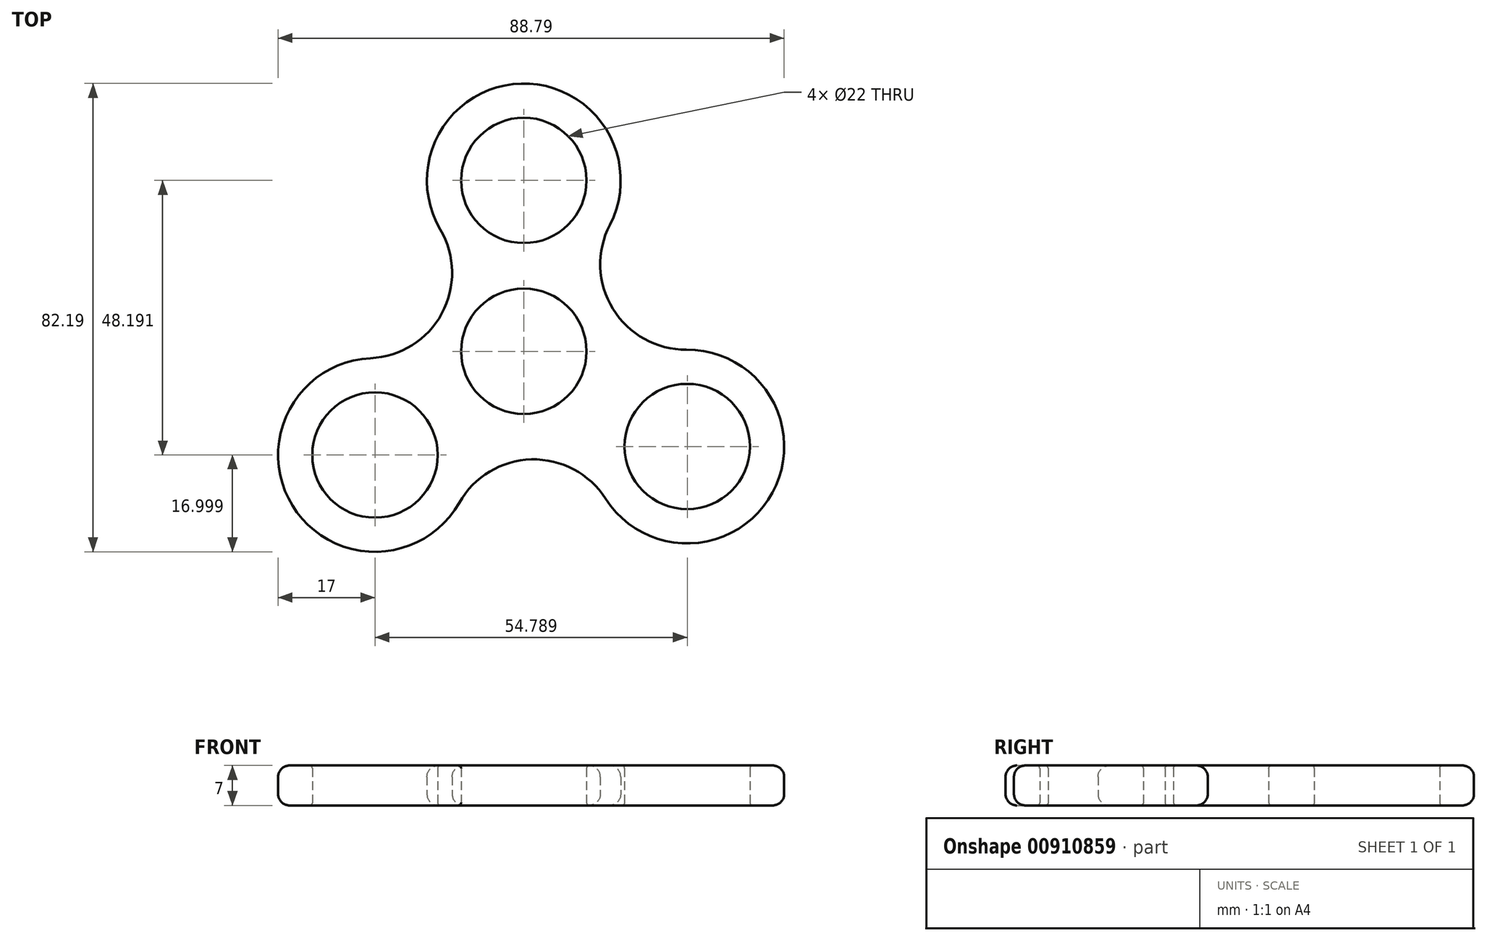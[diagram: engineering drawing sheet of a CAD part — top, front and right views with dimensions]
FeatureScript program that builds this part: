
annotation { "Feature Type Name" : "Feature", "Feature Type Description" : "" }
export const myFeature = defineFeature(function(context is Context, id is Id, definition is map)
    precondition{}
    {
        {
            var Q0;
            Q0=qCreatedBy(makeId("Top.planeOp"),FACE);
            var sketch = newSketch(context, id + "F0", { "sketchPlane" : qUnion([Q0])});
            skLineSegment(sketch, "E0", {"start": v(0, 0) * mm, "end": v(0, 30) * mm, "construction": true});
            skCircle(sketch, "E1", {"center": v(0, 0) * mm, "radius": 11 * mm});
            skCircle(sketch, "E2", {"center": v(0, 30) * mm, "radius": 11 * mm});
            skCircle(sketch, "E3.1.1", {"center": v(-26.1, -18.2) * mm, "radius": 11 * mm});
            skCircle(sketch, "E3.2.1", {"center": v(28.68, -16.7) * mm, "radius": 11 * mm});
            skPoint(sketch, "E3.center", {"position": v(0.86, -1.63) * mm});
            skCircle(sketch, "E4.0", {"center": v(0, 30) * mm, "radius": 17 * mm});
            skCircle(sketch, "E5.0", {"center": v(-26.1, -18.2) * mm, "radius": 17 * mm});
            skCircle(sketch, "E6.0", {"center": v(28.68, -16.7) * mm, "radius": 17 * mm});
            skArc(sketch, "E7", {"start": v(-26.9, -1.2) * mm, "mid": v(-14.4, 6.63) * mm, "end": v(-14.65, 21.38) * mm});
            skArc(sketch, "E8", {"start": v(14.36, -25.88) * mm, "mid": v(1.33, -18.97) * mm, "end": v(-11.32, -26.57) * mm});
            skArc(sketch, "E9", {"start": v(15.1, 22.19) * mm, "mid": v(15.64, 7.44) * mm, "end": v(28.54, 0.3) * mm});
            skSolve(sketch);
        }
        {
            var Q0;
            Q0=makeQuery(id+"F0.imprint","IMPRINT",FACE,{"disambiguationData":[TD([[makeQuery(id+"F0.imprint","IMPRINT",EDGE,{"derivedFrom":sQuery(id+"F0.wireOp",EDGE,"E2")}),-1.0]])]});
            var Q1;
            Q1=makeQuery(id+"F0.imprint","IMPRINT",FACE,{"disambiguationData":[TD([[makeQuery(id+"F0.imprint","IMPRINT",EDGE,{"derivedFrom":sQuery(id+"F0.wireOp",EDGE,"E1")}),-1.0]])]});
            var Q2;
            Q2=makeQuery(id+"F0.imprint","IMPRINT",FACE,{"disambiguationData":[TD([[makeQuery(id+"F0.imprint","IMPRINT",EDGE,{"derivedFrom":sQuery(id+"F0.wireOp",EDGE,"E3.1.1")}),-1.0]])]});
            var Q3;
            Q3=makeQuery(id+"F0.imprint","IMPRINT",FACE,{"disambiguationData":[TD([[makeQuery(id+"F0.imprint","IMPRINT",EDGE,{"derivedFrom":sQuery(id+"F0.wireOp",EDGE,"E3.2.1")}),-1.0]])]});
            extrude(context, id + "F1", {"entities" : qUnion([Q0, Q1, Q2, Q3]), "endBound" : BoundingType.SYMMETRIC, "depth" : 7 * mm, "offsetDistance" : 25.4 * mm});
        }
        {
            var Q0;
            Q0=makeQuery(id+"F1.opExtrude","CAP_EDGE",EDGE,{"disambiguationData":[OSD([sQuery(id+"F0.wireOp",EDGE,"E4.0")])],"isStart":false});
            var Q1;
            Q1=makeQuery(id+"F1.opExtrude","CAP_EDGE",EDGE,{"disambiguationData":[OSD([sQuery(id+"F0.wireOp",EDGE,"E9")])],"isStart":false});
            var Q2;
            Q2=makeQuery(id+"F1.opExtrude","CAP_EDGE",EDGE,{"disambiguationData":[OSD([sQuery(id+"F0.wireOp",EDGE,"E6.0")])],"isStart":false});
            var Q3;
            Q3=makeQuery(id+"F1.opExtrude","CAP_EDGE",EDGE,{"disambiguationData":[OSD([sQuery(id+"F0.wireOp",EDGE,"E4.0")])],"isStart":true});
            fillet(context, id + "F2", {"entities" : qUnion([Q0, Q1, Q2, Q3]), "radius" : 2 * mm, "tangentPropagation" : true, "allowEdgeOverflow" : false});
        }
        {
            var Q0;
            Q0=makeQuery(id+"F1.opExtrude","CAP_EDGE",EDGE,{"disambiguationData":[OSD([sQuery(id+"F0.wireOp",EDGE,"E1")])],"isStart":false});
            var Q1;
            Q1=makeQuery(id+"F1.opExtrude","CAP_EDGE",EDGE,{"disambiguationData":[OSD([sQuery(id+"F0.wireOp",EDGE,"E3.2.1")])],"isStart":false});
            var Q2;
            Q2=makeQuery(id+"F1.opExtrude","CAP_EDGE",EDGE,{"disambiguationData":[OSD([sQuery(id+"F0.wireOp",EDGE,"E3.1.1")])],"isStart":false});
            var Q3;
            Q3=makeQuery(id+"F1.opExtrude","CAP_FACE",FACE,{"disambiguationData":[OSD([sQuery(id+"F0.wireOp",EDGE,"E1"),sQuery(id+"F0.wireOp",EDGE,"E2"),sQuery(id+"F0.wireOp",EDGE,"E3.1.1"),sQuery(id+"F0.wireOp",EDGE,"E3.2.1"),sQuery(id+"F0.wireOp",EDGE,"E4.0"),sQuery(id+"F0.wireOp",EDGE,"E5.0"),sQuery(id+"F0.wireOp",EDGE,"E6.0"),sQuery(id+"F0.wireOp",EDGE,"E7"),sQuery(id+"F0.wireOp",EDGE,"E8"),sQuery(id+"F0.wireOp",EDGE,"E9")])],"isStart":true});
            var Q4;
            Q4=makeQuery(id+"F1.opExtrude","CAP_EDGE",EDGE,{"disambiguationData":[OSD([sQuery(id+"F0.wireOp",EDGE,"E2")])],"isStart":false});
            fillet(context, id + "F3", {"entities" : qUnion([Q0, Q1, Q2, Q3, Q4]), "radius" : .5 * mm, "tangentPropagation" : true, "allowEdgeOverflow" : false});
        }
    });
